# Revit family: xRail_System-Zoeller-(6_Inch)
name_source: partatom
category: Mechanical Equipment
revit_build: Autodesk Revit 2014 (Build: 20130308_1515(x64)
units: mm (PartAtom-declared; Revit-internal decimal feet)

## types (2) — shared parameters
Assembly Code = D2030400
Bracket Height = 60"
CW Connection = Yes
Connection Type = 6" Horizontal Flange
Default Elevation = 60"
Description = 6" Guide Rail System SS
HW Connection = No
Manufacturer = Zoeller
Material = Metal-Zoeller-Powder Coated Cast Iron
Model = 6" Rail System
Non-Sparkling Rail System = Yes
Price = Prices may vary. Please consult Manufacturer Representative for most up-to-date price list.
Pump Discharge Diameter = 6"
Pump Discharge Radius = 3"
Rail System Discharge Diameter = 6"
Rail System Discharge Radius = 3"
URL = http://www.zoellerpumps.com
Vent Connection = No
Waste Connection = Yes

## per-type parameters (varying)
| type | Mounting Plate | Mounting Plate Material |
| 6039-0072 - 6" Rail System | Mounting_Plate-Zoeller-Rail_System-C00094 : C00094 - Mounting Plate - Cast Iron | Metal-Zoeller-Powder Coated Cast Iron |
| 6039-0073 - 6" Non-Sparking Rail System | Mounting_Plate-Zoeller-Rail_System-C00094 : C00094 - Mounting Plate - Brass | Brass-Zoeller-Copper Alloy |

## geometry (parser evidence)
native form markers: Sweep x5
no freeform markers — native parametric forms only
